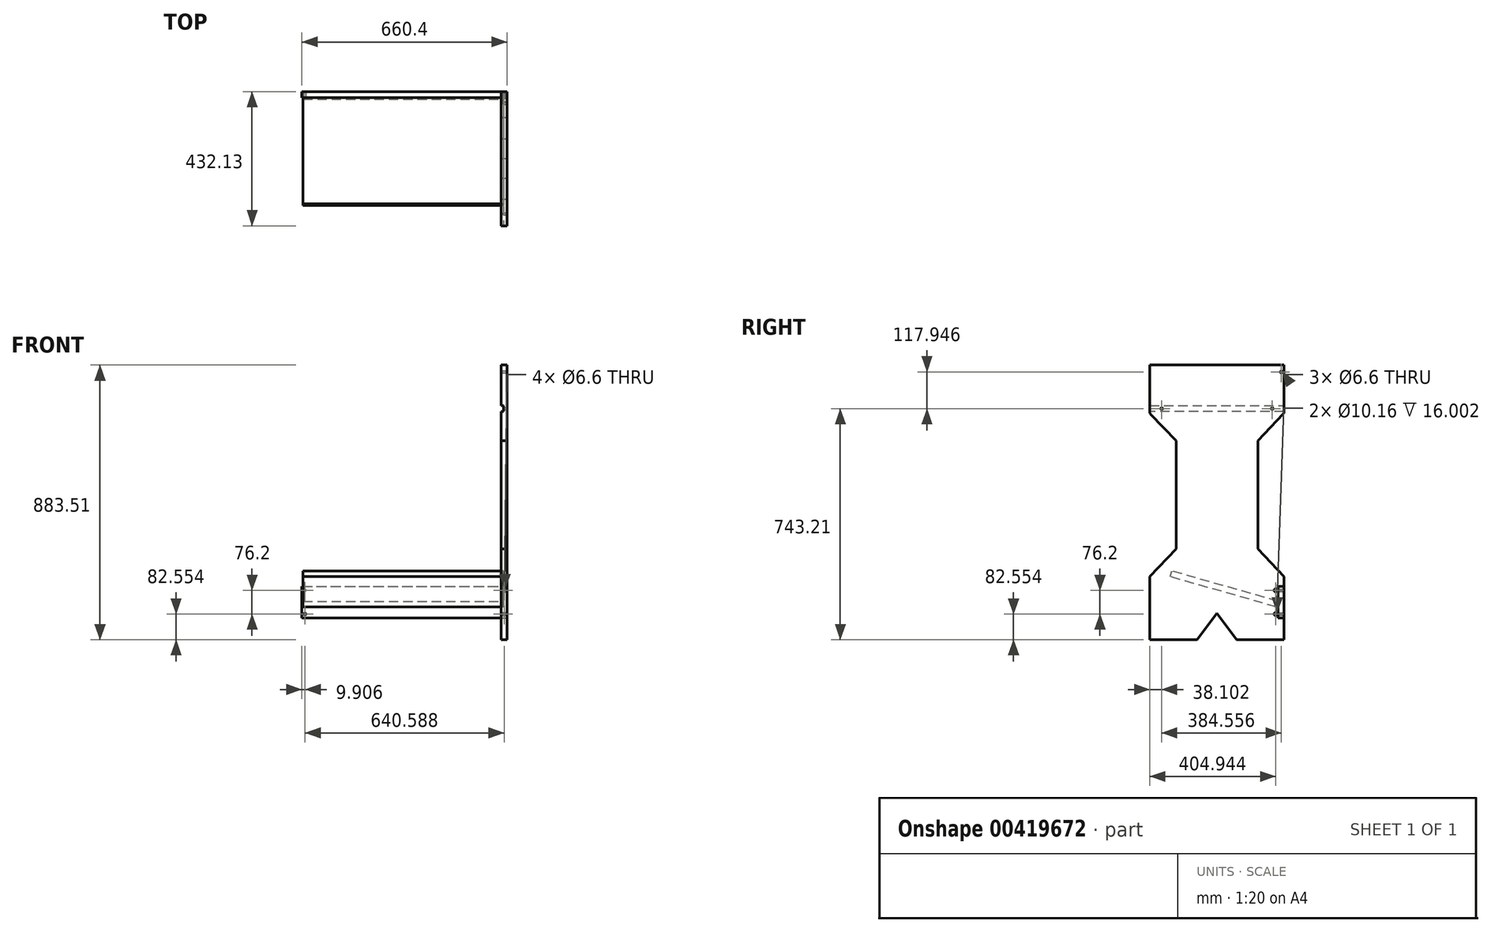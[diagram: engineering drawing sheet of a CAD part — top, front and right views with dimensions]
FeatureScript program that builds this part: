
annotation { "Feature Type Name" : "Feature", "Feature Type Description" : "" }
export const myFeature = defineFeature(function(context is Context, id is Id, definition is map)
    precondition{}
    {
        {
            var Q0;
            Q0=qCreatedBy(makeId("Right.planeOp"),FACE);
            var sketch = newSketch(context, id + "F0", { "sketchPlane" : qUnion([Q0])});
            skLineSegment(sketch, "E0.bottom", {"start": v(215.57, 77.66) * mm, "end": v(-216.23, 77.66) * mm});
            skLineSegment(sketch, "E0.left", {"start": v(215.57, 77.66) * mm, "end": v(215.57, -73.15) * mm});
            skLineSegment(sketch, "E0.right", {"start": v(-216.23, 77.66) * mm, "end": v(-216.23, -73.15) * mm});
            skPoint(sketch, "E0.middle", {"position": v(0, 0) * mm});
            skLineSegment(sketch, "E1", {"start": v(-213.41, -80.17) * mm, "end": v(-131.54, -165.77) * mm});
            skLineSegment(sketch, "E2", {"start": v(212.78, -80.14) * mm, "end": v(131.54, -165.77) * mm});
            skLineSegment(sketch, "E3", {"start": v(-131.54, -165.77) * mm, "end": v(-131.54, -513.75) * mm});
            skArc(sketch, "E4.filletArc", {"start": v(-216.23, -73.15) * mm, "mid": v(-215.5, -76.93) * mm, "end": v(-213.41, -80.17) * mm});
            skArc(sketch, "E5.filletArc", {"start": v(212.78, -80.14) * mm, "mid": v(214.85, -76.91) * mm, "end": v(215.57, -73.15) * mm});
            skLineSegment(sketch, "E6", {"start": v(-131.54, -513.75) * mm, "end": v(-215.9, -602.65) * mm});
            skLineSegment(sketch, "E7", {"start": v(-215.9, -602.65) * mm, "end": v(-215.9, -805.85) * mm});
            skLineSegment(sketch, "E8.MirrorCS", {"start": v(131.54, -165.77) * mm, "end": v(131.54, -513.75) * mm});
            skLineSegment(sketch, "E9.MirrorCS", {"start": v(131.54, -513.75) * mm, "end": v(215.9, -602.65) * mm});
            skLineSegment(sketch, "E10", {"start": v(-131.54, -165.77) * mm, "end": v(-34.69, -165.77) * mm, "construction": true});
            skLineSegment(sketch, "E11", {"start": v(-215.9, -602.65) * mm, "end": v(-131.54, -602.65) * mm, "construction": true});
            skLineSegment(sketch, "E12", {"start": v(-215.9, -805.85) * mm, "end": v(-63.5, -805.85) * mm});
            skLineSegment(sketch, "E13", {"start": v(-63.5, -805.85) * mm, "end": v(0, -721.49) * mm});
            skLineSegment(sketch, "E14", {"start": v(0, -721.49) * mm, "end": v(63.5, -805.85) * mm});
            skLineSegment(sketch, "E15", {"start": v(63.5, -805.85) * mm, "end": v(215.9, -805.85) * mm});
            skPoint(sketch, "E16", {"position": v(215.9, -634.4) * mm});
            skPoint(sketch, "E17", {"position": v(215.9, -736) * mm});
            skLineSegment(sketch, "E18", {"start": v(215.9, -634.4) * mm, "end": v(196.85, -634.4) * mm});
            skLineSegment(sketch, "E19", {"start": v(196.85, -634.4) * mm, "end": v(196.85, -736) * mm});
            skLineSegment(sketch, "E20", {"start": v(196.85, -736) * mm, "end": v(215.9, -736) * mm});
            skLineSegment(sketch, "E21", {"start": v(215.9, -602.65) * mm, "end": v(215.9, -634.4) * mm});
            skLineSegment(sketch, "E22", {"start": v(215.9, -736) * mm, "end": v(215.9, -805.85) * mm});
            skSolve(sketch);
        }
        {
            var Q0;
            Q0=qSketchRegion(id+"F0",true);
            extrude(context, id + "F1", {"entities" : qUnion([Q0]), "depth" : 19.05 * mm});
        }
        {
            var Q0;
            Q0=makeQuery(id+"F1.opExtrude","CAP_FACE",FACE,{"disambiguationData":[OSD([sQuery(id+"F0.wireOp",EDGE,"E0.bottom"),sQuery(id+"F0.wireOp",EDGE,"E0.left"),sQuery(id+"F0.wireOp",EDGE,"E0.right"),sQuery(id+"F0.wireOp",EDGE,"E1"),sQuery(id+"F0.wireOp",EDGE,"E2"),sQuery(id+"F0.wireOp",EDGE,"E3"),sQuery(id+"F0.wireOp",EDGE,"E4.filletArc"),sQuery(id+"F0.wireOp",EDGE,"E5.filletArc"),sQuery(id+"F0.wireOp",EDGE,"E6"),sQuery(id+"F0.wireOp",EDGE,"E7"),sQuery(id+"F0.wireOp",EDGE,"E8.MirrorCS"),sQuery(id+"F0.wireOp",EDGE,"E9.MirrorCS"),sQuery(id+"F0.wireOp",EDGE,"E12"),sQuery(id+"F0.wireOp",EDGE,"E13"),sQuery(id+"F0.wireOp",EDGE,"E14"),sQuery(id+"F0.wireOp",EDGE,"E15"),sQuery(id+"F0.wireOp",EDGE,"E18"),sQuery(id+"F0.wireOp",EDGE,"E19"),sQuery(id+"F0.wireOp",EDGE,"E20"),sQuery(id+"F0.wireOp",EDGE,"E21"),sQuery(id+"F0.wireOp",EDGE,"E22")])],"isStart":false});
            var sketch = newSketch(context, id + "F2", { "sketchPlane" : qUnion([Q0])});
            skLineSegment(sketch, "E23.bottom", {"start": v(215.9, -736) * mm, "end": v(196.84, -736) * mm});
            skLineSegment(sketch, "E23.top", {"start": v(215.9, -634.4) * mm, "end": v(196.84, -634.4) * mm});
            skLineSegment(sketch, "E23.left", {"start": v(215.9, -736) * mm, "end": v(215.9, -634.4) * mm});
            skLineSegment(sketch, "E23.right", {"start": v(196.84, -736) * mm, "end": v(196.84, -634.4) * mm});
            skSolve(sketch);
        }
        {
            var Q0;
            Q0=qSketchRegion(id+"F2",true);
            extrude(context, id + "F3", {"entities" : qUnion([Q0]), "oppositeDirection" : true, "depth" : 660.4 * mm});
        }
        {
            var Q0;
            Q0=makeQuery(id+"F0.imprint","IMPRINT",FACE,{"disambiguationData":[TD([[makeQuery(id+"F0.imprint","IMPRINT",EDGE,{"derivedFrom":sQuery(id+"F0.wireOp",EDGE,"E0.bottom")}),1.0]])]});
            var sketch = newSketch(context, id + "F4", { "sketchPlane" : qUnion([Q0])});
            skLineSegment(sketch, "E24", {"start": v(196.84, -682.6) * mm, "end": v(191.6, -700.92) * mm});
            skLineSegment(sketch, "E25", {"start": v(191.6, -700.92) * mm, "end": v(-150.3, -603.22) * mm});
            skLineSegment(sketch, "E26", {"start": v(-150.3, -603.22) * mm, "end": v(-145.07, -584.9) * mm});
            skLineSegment(sketch, "E27", {"start": v(196.84, -682.6) * mm, "end": v(-145.07, -584.9) * mm});
            skSolve(sketch);
        }
        {
            var Q0;
            Q0=makeQuery(id+"F4.imprint","IMPRINT",FACE,{"disambiguationData":[TD([[makeQuery(id+"F4.imprint","IMPRINT",EDGE,{"derivedFrom":sQuery(id+"F4.wireOp",EDGE,"E24")}),-1.0]])]});
            extrude(context, id + "F5", {"entities" : qUnion([Q0]), "operationType" : NewBodyOperationType.REMOVE, "depth" : 7.62 * mm});
        }
        {
            var Q0;
            Q0=makeQuery(id+"F0.imprint","IMPRINT",FACE,{"disambiguationData":[TD([[makeQuery(id+"F0.imprint","IMPRINT",EDGE,{"derivedFrom":sQuery(id+"F0.wireOp",EDGE,"E0.bottom")}),1.0]])]});
            var sketch = newSketch(context, id + "F6", { "sketchPlane" : qUnion([Q0])});
            skLineSegment(sketch, "E28", {"start": v(216.17, -71.28) * mm, "end": v(-216.23, -71.28) * mm});
            skLineSegment(sketch, "E29", {"start": v(-216.23, -71.28) * mm, "end": v(-216.23, -52.23) * mm});
            skLineSegment(sketch, "E30", {"start": v(-216.23, -52.23) * mm, "end": v(215.57, -52.23) * mm});
            skLineSegment(sketch, "E31", {"start": v(215.57, -52.23) * mm, "end": v(216.17, -71.28) * mm});
            skSolve(sketch);
        }
        {
            var Q0;
            Q0=qSketchRegion(id+"F6",true);
            extrude(context, id + "F7", {"entities" : qUnion([Q0]), "operationType" : NewBodyOperationType.REMOVE, "depth" : 7.62 * mm});
        }
        {
            var Q0;
            Q0=makeQuery(id+"F0.imprint","IMPRINT",FACE,{"disambiguationData":[TD([[makeQuery(id+"F0.imprint","IMPRINT",EDGE,{"derivedFrom":sQuery(id+"F0.wireOp",EDGE,"E0.bottom")}),1.0]])]});
            var sketch = newSketch(context, id + "F8", { "sketchPlane" : qUnion([Q0])});
            skLineSegment(sketch, "E32", {"start": v(196.84, -682.6) * mm, "end": v(191.6, -700.92) * mm});
            skLineSegment(sketch, "E33", {"start": v(191.6, -700.92) * mm, "end": v(-150.3, -603.22) * mm});
            skLineSegment(sketch, "E34", {"start": v(-150.3, -603.22) * mm, "end": v(-145.07, -584.9) * mm});
            skLineSegment(sketch, "E35", {"start": v(196.84, -682.6) * mm, "end": v(-145.07, -584.9) * mm});
            skSolve(sketch);
        }
        {
            var Q0;
            Q0=qSketchRegion(id+"F8",true);
            extrude(context, id + "F9", {"entities" : qUnion([Q0]), "oppositeDirection" : true, "depth" : 637.54 * mm});
        }
        {
            var Q0;
            Q0=makeQuery(id+"F3.opExtrude","SWEPT_FACE",FACE,{"disambiguationData":[OSD([sQuery(id+"F2.wireOp",EDGE,"E23.left")])]});
            var sketch = newSketch(context, id + "F10", { "sketchPlane" : qUnion([Q0])});
            skCircle(sketch, "E36", {"center": v(-9.14, -647.1) * mm, "radius": 3.3 * mm});
            skCircle(sketch, "E37", {"center": v(-9.14, -723.3) * mm, "radius": 3.3 * mm});
            skCircle(sketch, "E38", {"center": v(631.44, -647.1) * mm, "radius": 3.3 * mm});
            skCircle(sketch, "E39", {"center": v(631.44, -723.3) * mm, "radius": 3.3 * mm});
            skSolve(sketch);
        }
        {
            var Q0;
            Q0 = qSketchRegion(id + "F10", true);
            extrude(context, id + "F11", {"entities" : qUnion([Q0]), "operationType" : NewBodyOperationType.REMOVE, "oppositeDirection" : true, "depth" : 19.05 * mm});
        }
        {
            var Q0;
            {var subQ7=sQuery(id+"F2.wireOp",EDGE,"E23.right");Q0=makeQuery(id+"F2.imprint","IMPRINT",FACE,{"disambiguationData":[TD([[makeQuery(id+"F2.imprint","IMPRINT",EDGE,{"derivedFrom":subQ7}),1.0]])]});}
            var sketch = newSketch(context, id + "F12", { "sketchPlane" : qUnion([Q0])});
            skCircle(sketch, "E40", {"center": v(177.47, -62.64) * mm, "radius": 3.3 * mm});
            skCircle(sketch, "E41", {"center": v(-178.13, -62.64) * mm, "radius": 3.3 * mm});
            skCircle(sketch, "E42", {"center": v(206.43, 55.3) * mm, "radius": 3.3 * mm});
            skSolve(sketch);
        }
        {
            var Q0;
            Q0 = qSketchRegion(id + "F12", true);
            extrude(context, id + "F13", {"entities" : qUnion([Q0]), "operationType" : NewBodyOperationType.REMOVE, "oppositeDirection" : true, "depth" : 19.05 * mm});
        }
        {
            var Q0;
            Q0=makeQuery(id+"F12.imprint","IMPRINT",FACE,{"disambiguationData":[TD([[makeQuery(id+"F12.imprint","IMPRINT",EDGE,{"derivedFrom":sQuery(id+"F12.wireOp",EDGE,"E40")}),-1.0]])]});
            var sketch = newSketch(context, id + "F14", { "sketchPlane" : qUnion([Q0])});
            skPoint(sketch, "E43", {"position": v(215.9, -647.1) * mm});
            skPoint(sketch, "E44", {"position": v(215.9, -723.3) * mm});
            skCircle(sketch, "E45", {"center": v(188.71, -723.3) * mm, "radius": 5.08 * mm});
            skCircle(sketch, "E46", {"center": v(188.71, -647.1) * mm, "radius": 5.08 * mm});
            skPoint(sketch, "E47", {"position": v(196.84, -634.4) * mm});
            skLineSegment(sketch, "E48", {"start": v(196.84, -634.4) * mm, "end": v(188.71, -634.4) * mm, "construction": true});
            skLineSegment(sketch, "E49", {"start": v(188.71, -634.4) * mm, "end": v(188.71, -647.1) * mm, "construction": true});
            skLineSegment(sketch, "E50", {"start": v(189.48, -736) * mm, "end": v(196.85, -736) * mm, "construction": true});
            skSolve(sketch);
        }
        {
            var Q0;
            Q0 = qSketchRegion(id + "F14", true);
            extrude(context, id + "F15", {"entities" : qUnion([Q0]), "operationType" : NewBodyOperationType.REMOVE, "oppositeDirection" : true, "depth" : 16 * mm});
        }
    });
